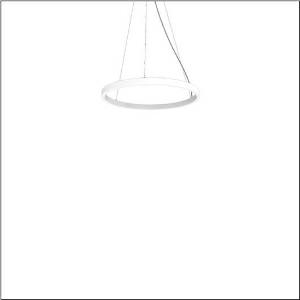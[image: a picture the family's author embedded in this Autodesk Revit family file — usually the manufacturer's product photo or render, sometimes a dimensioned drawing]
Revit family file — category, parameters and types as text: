
# Revit family: silica_21_ring-o_5pjbo1d1004a
name_source: partatom
category: Lighting Fixtures
units: mm (PartAtom-declared; Revit-internal decimal feet)

## family parameters
Cut with Voids When Loaded = No
Host = Face
Light Source = No
Part Type = Normal
Room Calculation Point = No
Round Connector Dimension = Use Diameter
Shared = No

## types (1)
- Silica 21 Ring-O (1 x LED, 3740 lm, 60 W, 3000K)
    Apparent Load = 60 VA
    CIE Flux Codes = 2 16 49 50 100
    Color Rendering = 80
    Color Temperature = 3000K
    Default Elevation = 1800 mm
    Description = Silica 21 Ring-O, suspended luminaire, of PMMA, frosted, light emission: outer ring side luminous distribution, primary light characteristic: symmetric, installation type: suspended mounting, LED, rated luminous flux: 3.744lm, luminous efficacy: 62lm/W, light colour: 830, colour temperature: 3000K, control gear: DALI 2, with terminal, 5-pole, mains connection: 230V, AC/DC, 0/50..60Hz, rated input power: 60W, housing, of extruded aluminium section, traffic white (RAL 9016), diameter: 610mm, ceiling canopy, traffic white (RAL 9016), protection rating (lamp compartment): IP40, insulation class (complete): insulation class I (protective earthing), certification: CE, impact resistance: IK02, permissible operating ambient temperature: 0..+35°C, packaging unit: 1 piece
    Height = 48 mm  [stored 0.15748 ft]
    Lamp = 1 x LED
    Lamp Light Flux = 3740 lm
    Lamp Power = 60 W
    Lamp count = 1
    Length = 610 mm
    Luminous efficacy = 62 lm/W
    Manufacturer = Siteco
    ModVariant = No
    Model = 5PJBO1D1004A
    Mounting Place = Ceiling
    Mounting Type = Pendant
    Number of Poles = 1
    OnlyDefault = Yes
    Power Factor = 1
    Product Name = Silica 21 Ring-O
    Product group = suspended luminaire
    ProductGroupID = 904
    Protection Class = Protection class I
    Protection Degree = IP 40
    RLX_Detail_Level = 1
    RLX_Emergency_Light_Flux = 0 lm
    RLX_Emergency_Type = 0
    RLX_Emergency_Type_DB = No
    RlxData = <blob elided: 10581 chars, md5=5c4307da>
    Socket = socket
    Standby Power = 0 W
    System Light Flux = 3740 lm
    System Power = 60 W
    Type Comments = Product without accessories
    Type Image = l_1258379.jpg
    URL = http://relux.com
    VarID = ---
    Voltage = 0 V
    Weight = 0.00 kg
    Width = 0 mm  [stored 0 ft]

note: [stored X ft] marks values corroborated as IEEE doubles in the binary element streams (Revit-internal decimal feet)

## geometry (parser evidence)
native form markers: Sweep x11
no freeform markers — native parametric forms only
